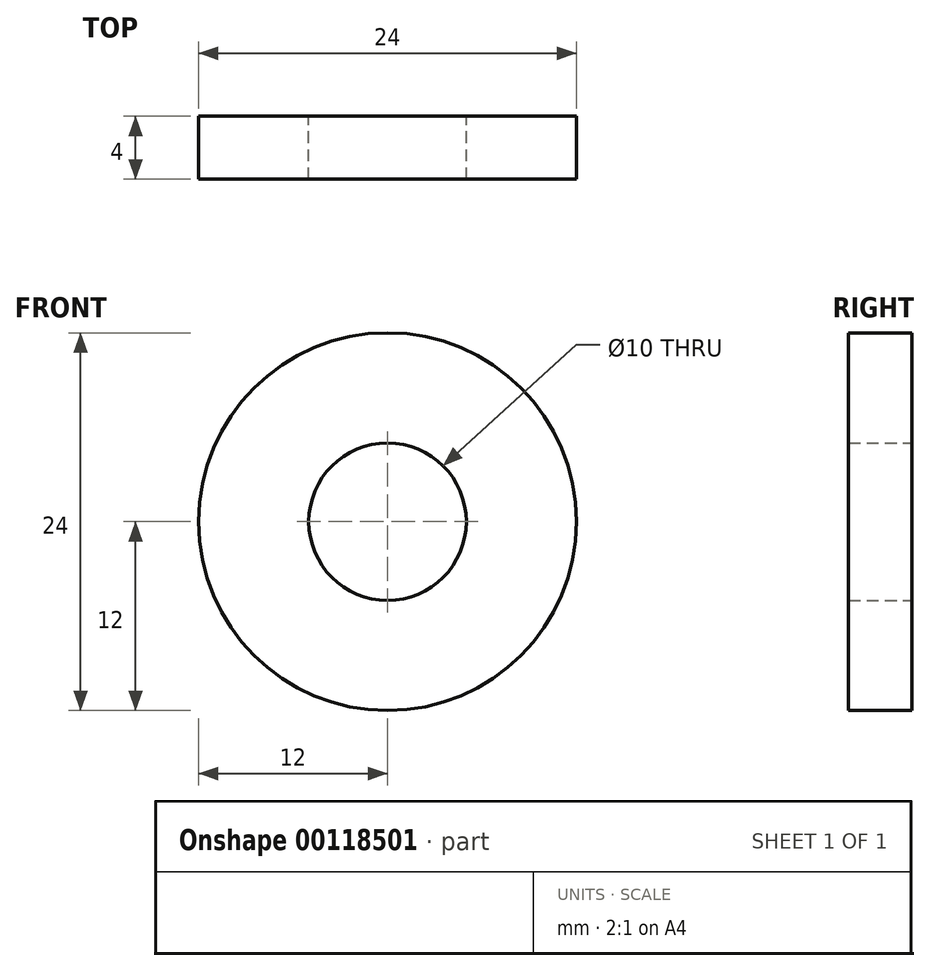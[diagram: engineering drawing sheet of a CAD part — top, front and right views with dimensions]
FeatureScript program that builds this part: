
annotation { "Feature Type Name" : "Feature", "Feature Type Description" : "" }
export const myFeature = defineFeature(function(context is Context, id is Id, definition is map)
    precondition{}
    {
        {
            var Q0;
            Q0=qCreatedBy(makeId("Front.planeOp"),FACE);
            var sketch = newSketch(context, id + "F0", { "sketchPlane" : qUnion([Q0])});
            skCircle(sketch, "E0", {"center": v(0, 0) * mm, "radius": 5 * mm});
            skCircle(sketch, "E1", {"center": v(0, 0) * mm, "radius": 12 * mm});
            skSolve(sketch);
        }
        {
            var Q0;
            Q0=makeQuery(id+"F0.imprint","IMPRINT",FACE,{"disambiguationData":[TD([[makeQuery(id+"F0.imprint","IMPRINT",EDGE,{"derivedFrom":sQuery(id+"F0.wireOp",EDGE,"E0")}),-1.0]])]});
            extrude(context, id + "F1", {"entities" : qUnion([Q0]), "depth" : 4 * mm});
        }
    });
